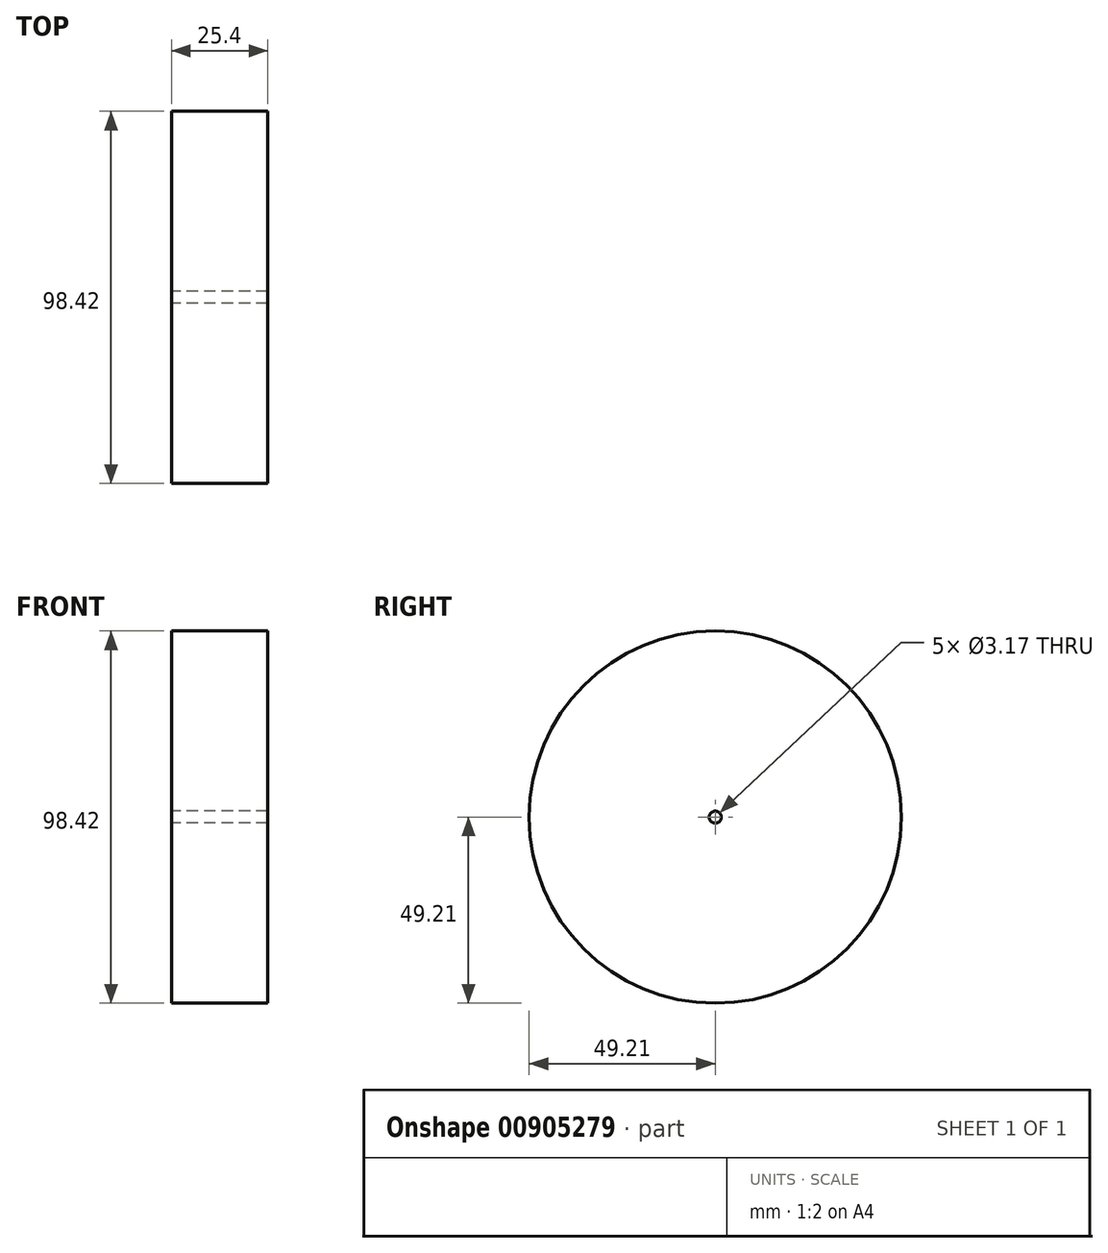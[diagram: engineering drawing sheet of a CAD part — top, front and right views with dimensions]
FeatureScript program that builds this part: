
annotation { "Feature Type Name" : "Feature", "Feature Type Description" : "" }
export const myFeature = defineFeature(function(context is Context, id is Id, definition is map)
    precondition{}
    {
        {
            var Q0;
            Q0=qCreatedBy(makeId("Right.planeOp"),FACE);
            var sketch = newSketch(context, id + "F0", { "sketchPlane" : qUnion([Q0])});
            skCircle(sketch, "E0", {"center": v(0, 0) * mm, "radius": 49.21 * mm});
            skCircle(sketch, "E1", {"center": v(0, 0) * mm, "radius": 1.59 * mm});
            skSolve(sketch);
        }
        {
            var Q0;
            Q0=makeQuery(id+"F0.imprint","IMPRINT",FACE,{"disambiguationData":[TD([[makeQuery(id+"F0.imprint","IMPRINT",EDGE,{"derivedFrom":sQuery(id+"F0.wireOp",EDGE,"E0")}),1.0]])]});
            extrude(context, id + "F1", {"entities" : qUnion([Q0]), "depth" : 25.4 * mm, "offsetDistance" : 25.4 * mm});
        }
    });
